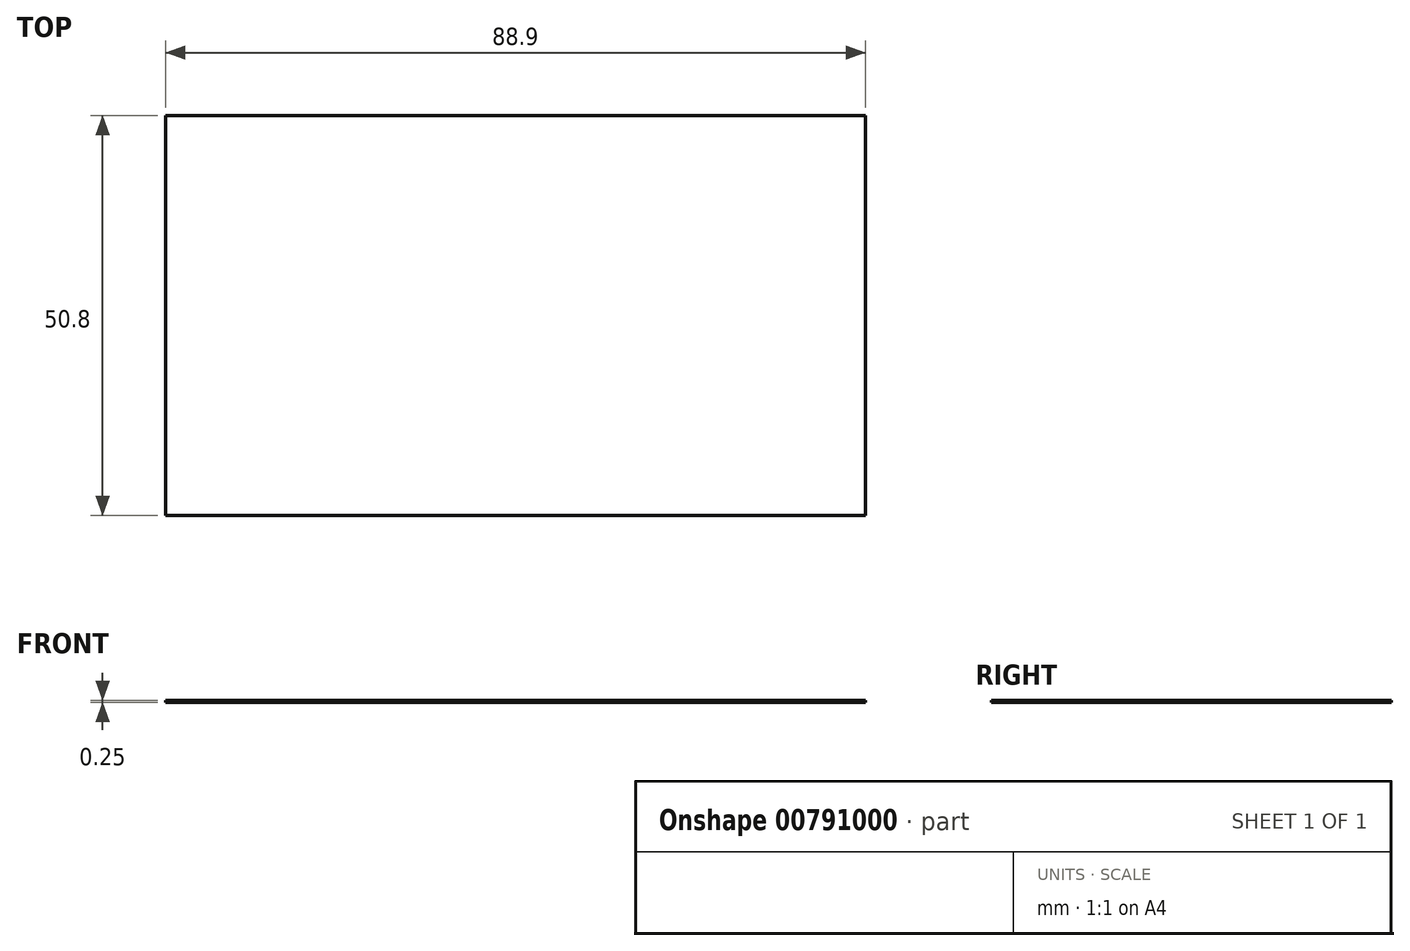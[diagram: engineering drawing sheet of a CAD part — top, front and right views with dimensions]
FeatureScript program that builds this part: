
annotation { "Feature Type Name" : "Feature", "Feature Type Description" : "" }
export const myFeature = defineFeature(function(context is Context, id is Id, definition is map)
    precondition{}
    {
        {
            var Q0;
            Q0=qCreatedBy(makeId("Top.planeOp"),FACE);
            var sketch = newSketch(context, id + "F0", { "sketchPlane" : qUnion([Q0])});
            skLineSegment(sketch, "E0.bottom", {"start": v(-44.45, 25.4) * mm, "end": v(44.45, 25.4) * mm});
            skLineSegment(sketch, "E0.top", {"start": v(-44.45, -25.4) * mm, "end": v(44.45, -25.4) * mm});
            skLineSegment(sketch, "E0.left", {"start": v(-44.45, 25.4) * mm, "end": v(-44.45, -25.4) * mm});
            skLineSegment(sketch, "E0.right", {"start": v(44.45, 25.4) * mm, "end": v(44.45, -25.4) * mm});
            skPoint(sketch, "E0.middle", {"position": v(0, 0) * mm});
            skSolve(sketch);
        }
        {
            var Q0;
            Q0 = qSketchRegion(id + "F0", true);
            extrude(context, id + "F1", {"entities" : qUnion([Q0]), "depth" : 0.25 * mm, "offsetDistance" : 25.4 * mm});
        }
    });
